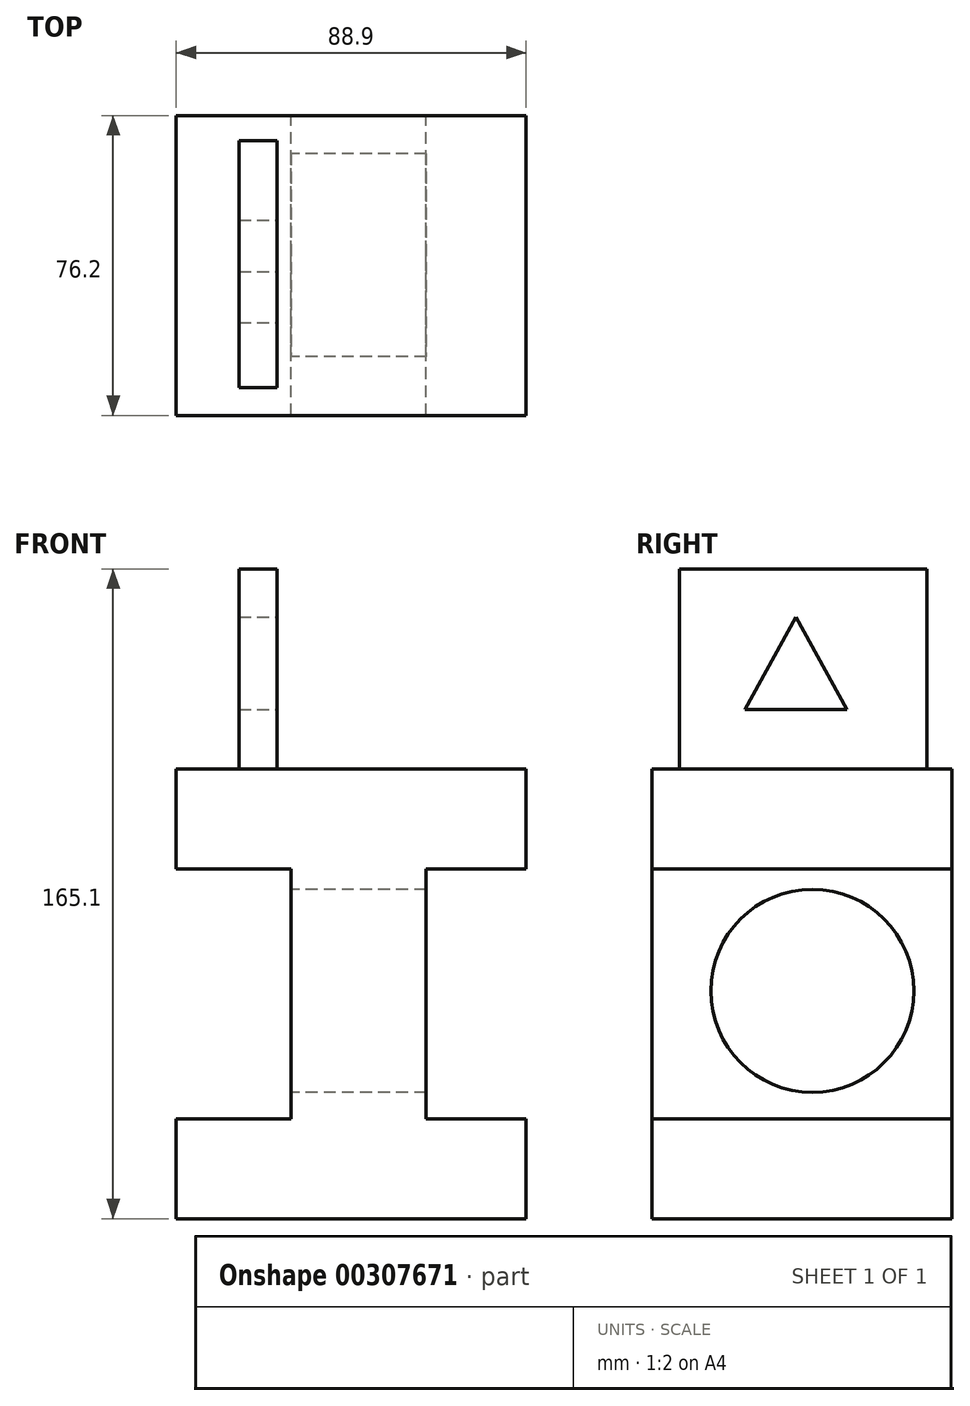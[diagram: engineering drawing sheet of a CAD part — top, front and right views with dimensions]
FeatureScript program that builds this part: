
annotation { "Feature Type Name" : "Feature", "Feature Type Description" : "" }
export const myFeature = defineFeature(function(context is Context, id is Id, definition is map)
    precondition{}
    {
        {
            var Q0;
            Q0=qCreatedBy(makeId("Front.planeOp"),FACE);
            var sketch = newSketch(context, id + "F0", { "sketchPlane" : qUnion([Q0])});
            skLineSegment(sketch, "E0", {"start": v(-44.6, -50.8) * mm, "end": v(44.3, -50.8) * mm});
            skLineSegment(sketch, "E1", {"start": v(44.3, -50.8) * mm, "end": v(44.3, -25.4) * mm});
            skLineSegment(sketch, "E2", {"start": v(44.3, -25.4) * mm, "end": v(18.9, -25.4) * mm});
            skLineSegment(sketch, "E3", {"start": v(18.9, -25.4) * mm, "end": v(18.9, 38.1) * mm});
            skLineSegment(sketch, "E4", {"start": v(18.9, 38.1) * mm, "end": v(44.3, 38.1) * mm});
            skLineSegment(sketch, "E5", {"start": v(44.3, 38.1) * mm, "end": v(44.3, 63.5) * mm});
            skLineSegment(sketch, "E6", {"start": v(44.3, 63.5) * mm, "end": v(-44.6, 63.5) * mm});
            skLineSegment(sketch, "E7", {"start": v(-44.6, 63.5) * mm, "end": v(-44.6, 38.1) * mm});
            skLineSegment(sketch, "E8", {"start": v(-44.6, 38.1) * mm, "end": v(-15.43, 38.1) * mm});
            skLineSegment(sketch, "E9", {"start": v(-15.43, 38.1) * mm, "end": v(-15.43, -25.4) * mm});
            skLineSegment(sketch, "E10", {"start": v(-15.43, -25.4) * mm, "end": v(-44.6, -25.4) * mm});
            skLineSegment(sketch, "E11", {"start": v(-44.6, -25.4) * mm, "end": v(-44.6, -50.8) * mm});
            skSolve(sketch);
        }
        {
            var Q0;
            Q0=makeQuery(id+"F0.imprint","IMPRINT",FACE,{"disambiguationData":[TD([[makeQuery(id+"F0.imprint","IMPRINT",EDGE,{"derivedFrom":sQuery(id+"F0.wireOp",EDGE,"E0")}),1.0]])]});
            extrude(context, id + "F1", {"entities" : qUnion([Q0]), "depth" : 76.2 * mm});
        }
        {
            var Q0;
            Q0=makeQuery(id+"F1.opExtrude","SWEPT_FACE",FACE,{"disambiguationData":[OSD([sQuery(id+"F0.wireOp",EDGE,"E6")])]});
            var sketch = newSketch(context, id + "F2", { "sketchPlane" : qUnion([Q0])});
            skLineSegment(sketch, "E12.bottom", {"start": v(-19.04, -69.2) * mm, "end": v(-28.63, -69.2) * mm});
            skLineSegment(sketch, "E12.top", {"start": v(-19.04, -6.37) * mm, "end": v(-28.63, -6.37) * mm});
            skLineSegment(sketch, "E12.left", {"start": v(-19.04, -69.2) * mm, "end": v(-19.04, -6.37) * mm});
            skLineSegment(sketch, "E12.right", {"start": v(-28.63, -69.2) * mm, "end": v(-28.63, -6.37) * mm});
            skSolve(sketch);
        }
        {
            var Q0;
            Q0=makeQuery(id+"F2.imprint","IMPRINT",FACE,{"disambiguationData":[TD([[makeQuery(id+"F2.imprint","IMPRINT",EDGE,{"derivedFrom":sQuery(id+"F2.wireOp",EDGE,"E12.bottom")}),-1.0]])]});
            extrude(context, id + "F3", {"entities" : qUnion([Q0]), "operationType" : NewBodyOperationType.ADD, "depth" : 50.8 * mm});
        }
        {
            var Q0;
            Q0=makeQuery(id+"F3.opExtrude","SWEPT_FACE",FACE,{"disambiguationData":[OSD([sQuery(id+"F2.wireOp",EDGE,"E12.left")])]});
            var sketch = newSketch(context, id + "F4", { "sketchPlane" : qUnion([Q0])});
            skLineSegment(sketch, "E13", {"start": v(-26.65, 78.53) * mm, "end": v(-52.65, 78.53) * mm});
            skLineSegment(sketch, "E14", {"start": v(-52.65, 78.53) * mm, "end": v(-39.65, 102.05) * mm});
            skPoint(sketch, "E14.endSnap0", {"position": v(-39.65, 78.53) * mm});
            skLineSegment(sketch, "E15", {"start": v(-39.65, 102.05) * mm, "end": v(-26.65, 78.53) * mm});
            skSolve(sketch);
        }
        {
            var Q0;
            Q0=makeQuery(id+"F4.imprint","IMPRINT",FACE,{"disambiguationData":[TD([[makeQuery(id+"F4.imprint","IMPRINT",EDGE,{"derivedFrom":sQuery(id+"F4.wireOp",EDGE,"E13")}),-1.0]])]});
            var Q1;
            Q1=sQuery(id+"F4.wireOp",EDGE,"E14");
            var Q2;
            Q2=sQuery(id+"F4.wireOp",EDGE,"E15");
            var Q3;
            Q3=sQuery(id+"F4.wireOp",EDGE,"E13");
            extrude(context, id + "F5", {"entities" : qUnion([Q0]), "operationType" : NewBodyOperationType.REMOVE, "surfaceEntities" : qUnion([Q1, Q2, Q3]), "endBound" : BoundingType.THROUGH_ALL, "oppositeDirection" : true, "depth" : 25.4 * mm});
        }
        {
            var Q0;
            Q0=makeQuery(id+"F1.opExtrude","SWEPT_FACE",FACE,{"disambiguationData":[OSD([sQuery(id+"F0.wireOp",EDGE,"E9")])]});
            var sketch = newSketch(context, id + "F6", { "sketchPlane" : qUnion([Q0])});
            skCircle(sketch, "E16", {"center": v(35.49, 7.09) * mm, "radius": 25.8 * mm});
            skSolve(sketch);
        }
        {
            var Q0;
            Q0=makeQuery(id+"F6.imprint","IMPRINT",FACE,{"disambiguationData":[TD([[makeQuery(id+"F6.imprint","IMPRINT",EDGE,{"derivedFrom":sQuery(id+"F6.wireOp",EDGE,"E16")}),1.0]])]});
            extrude(context, id + "F7", {"entities" : qUnion([Q0]), "operationType" : NewBodyOperationType.REMOVE, "endBound" : BoundingType.THROUGH_ALL, "oppositeDirection" : true, "depth" : 25.4 * mm});
        }
    });
